# Revit family: Valves-American_Standard-Town_Square-T455430
name_source: partatom
category: Plumbing Fixtures
revit_build: Autodesk Revit 2014 (Build: 20130308_1515(x64)
units: mm (PartAtom-declared; Revit-internal decimal feet)

## types (1)
- T455430
    ADA Compliant = Yes
    Assembly Code = D2020300
    Bath = Yes
    CW Connection = Yes
    CWFU = 3
    Default Elevation = 40"
    Description = TOWN SQUARE® S IN-WALL DIVERTER VALVES
    Finish = Metal-American Standard-002-Polished Chrome
    HW Connection = Yes
    HWFU = 3
    Height = 3 3/16"
    Installation Type = Wall Mounted
    Length = 3 1/4"
    Manufacturer = American Standard
    Material = Metal-American Standard-002-Polished Chrome
    Model = T455430
    Price = Prices may vary. Please consult Manufacturer Representative for most up-to-date price list.
    Product Documentation Link = https://www.americanstandard-us.com
    Product Page URL = https://www.americanstandard-us.com
    Shower = Yes
    Spacing from Wall = 1 5/8"
    Specification = Two (three) way diverter shall feature a forged brass body with 1/2” NPT mixed water inlet and outlets.
    URL = https://www.americanstandard-us.com
    Valve = Yes
    Valve To Shower Connection = 1/2"
    Valve To Shower Connection Description = 1/2'' NPT Shower Supply Outlet
    Valve To Spout Connection = 1/2"
    Valve To Spout Connection Description = 1/2'' NPT Spout Supply Outlet
    Vent Connection = No
    WFU = 4
    Warranty Information = One Year Limited Warranty
    Waste Connection = Yes
    Water Connection Diameter = 1/2"
    Width = 3 1/4"

## geometry (parser evidence)
native form markers: Sweep x3
no freeform markers — native parametric forms only
